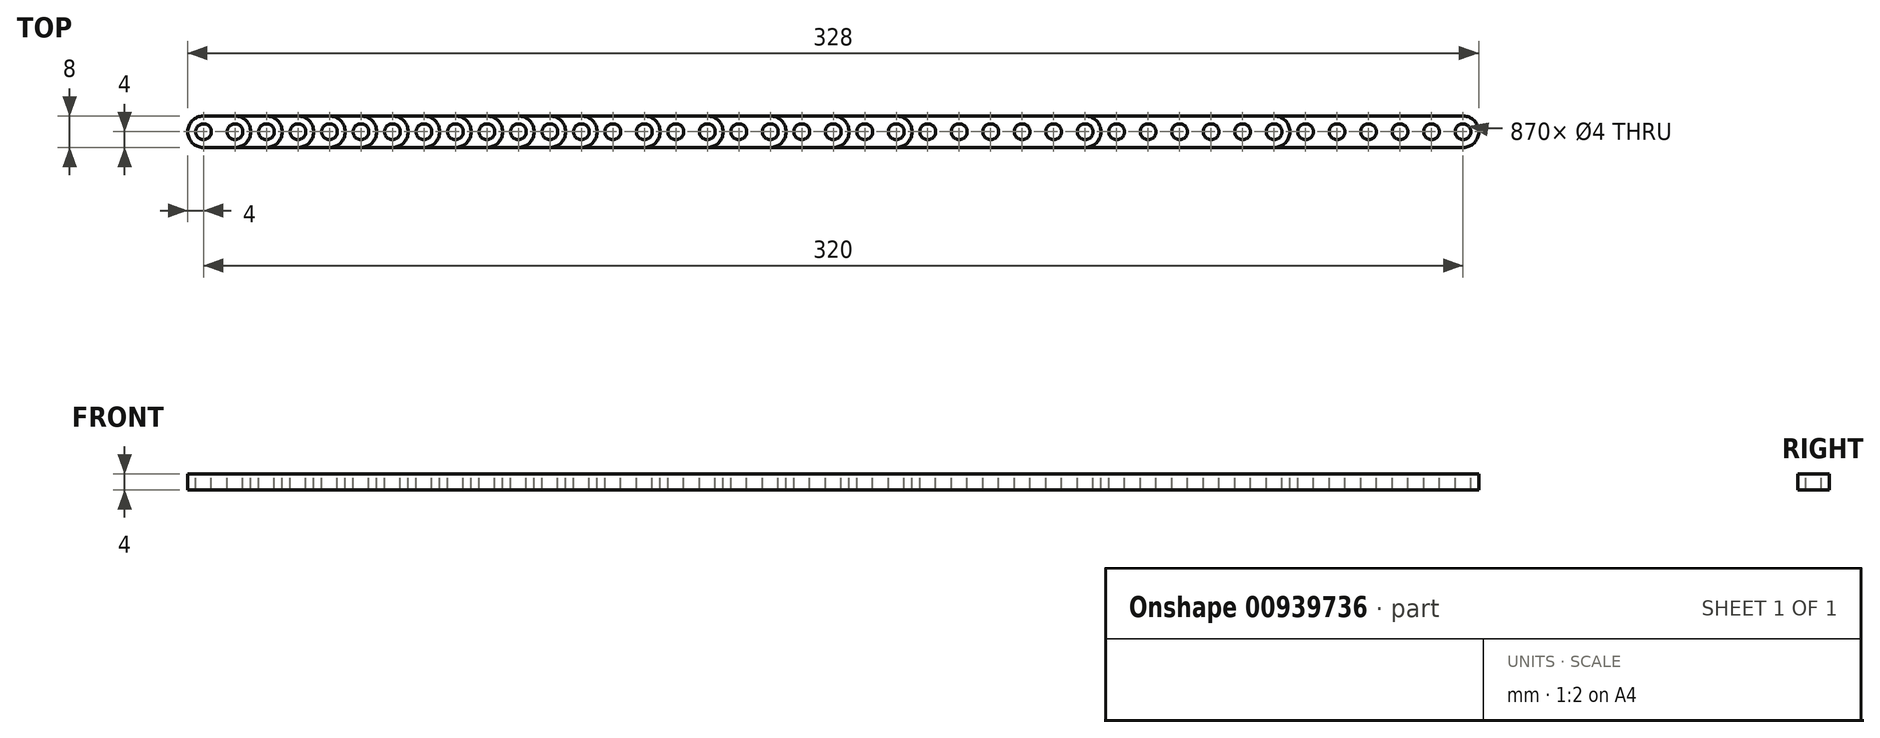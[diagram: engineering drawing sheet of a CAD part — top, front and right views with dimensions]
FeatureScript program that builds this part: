
annotation { "Feature Type Name" : "Feature", "Feature Type Description" : "" }
export const myFeature = defineFeature(function(context is Context, id is Id, definition is map)
    precondition{}
    {
        {
            var Q0;
            Q0=qCreatedBy(makeId("Right.planeOp"),FACE);
            var sketch = newSketch(context, id + "F0", { "sketchPlane" : qUnion([Q0])});
            skLineSegment(sketch, "E0.bottom", {"start": v(4, 2) * mm, "end": v(-4, 2) * mm});
            skLineSegment(sketch, "E0.top", {"start": v(4, -2) * mm, "end": v(-4, -2) * mm});
            skLineSegment(sketch, "E0.left", {"start": v(4, 2) * mm, "end": v(4, -2) * mm});
            skLineSegment(sketch, "E0.right", {"start": v(-4, 2) * mm, "end": v(-4, -2) * mm});
            skPoint(sketch, "E0.middle", {"position": v(0, 0) * mm});
            skSolve(sketch);
        }
        {
            var Q0;
            Q0=qSketchRegion(id+"F0",true);
            extrude(context, id + "F1", {"entities" : qUnion([Q0]), "depth" : 16 * mm, "offsetDistance" : 25 * mm});
        }
        {
            var Q0;
            Q0=qSketchRegion(id+"F0",true);
            extrude(context, id + "F2", {"entities" : qUnion([Q0]), "depth" : 24 * mm, "offsetDistance" : 25 * mm});
        }
        {
            var Q0;
            Q0=qSketchRegion(id+"F0",true);
            extrude(context, id + "F3", {"entities" : qUnion([Q0]), "depth" : 32 * mm, "offsetDistance" : 25 * mm});
        }
        {
            var Q0;
            Q0=qSketchRegion(id+"F0",true);
            extrude(context, id + "F4", {"entities" : qUnion([Q0]), "depth" : 40 * mm, "offsetDistance" : 25 * mm});
        }
        {
            var Q0;
            Q0=qSketchRegion(id+"F0",true);
            extrude(context, id + "F5", {"entities" : qUnion([Q0]), "depth" : 48 * mm, "offsetDistance" : 25 * mm});
        }
        {
            var Q0;
            Q0=qSketchRegion(id+"F0",true);
            extrude(context, id + "F6", {"entities" : qUnion([Q0]), "depth" : 56 * mm, "offsetDistance" : 25 * mm});
        }
        {
            var Q0;
            Q0=qSketchRegion(id+"F0",true);
            extrude(context, id + "F7", {"entities" : qUnion([Q0]), "depth" : 64 * mm, "offsetDistance" : 25 * mm});
        }
        {
            var Q0;
            Q0=qSketchRegion(id+"F0",true);
            extrude(context, id + "F8", {"entities" : qUnion([Q0]), "depth" : 72 * mm, "offsetDistance" : 25 * mm});
        }
        {
            var Q0;
            Q0=qSketchRegion(id+"F0",true);
            extrude(context, id + "F9", {"entities" : qUnion([Q0]), "depth" : 80 * mm, "offsetDistance" : 25 * mm});
        }
        {
            var Q0;
            Q0=qSketchRegion(id+"F0",true);
            extrude(context, id + "F10", {"entities" : qUnion([Q0]), "depth" : 88 * mm, "offsetDistance" : 25 * mm});
        }
        {
            var Q0;
            Q0=qSketchRegion(id+"F0",true);
            extrude(context, id + "F11", {"entities" : qUnion([Q0]), "depth" : 96 * mm, "offsetDistance" : 25 * mm});
        }
        {
            var Q0;
            Q0=qSketchRegion(id+"F0",true);
            extrude(context, id + "F12", {"entities" : qUnion([Q0]), "depth" : 104 * mm, "offsetDistance" : 25 * mm});
        }
        {
            var Q0;
            Q0=qSketchRegion(id+"F0",true);
            extrude(context, id + "F13", {"entities" : qUnion([Q0]), "depth" : 120 * mm, "offsetDistance" : 25 * mm});
        }
        {
            var Q0;
            Q0=qSketchRegion(id+"F0",true);
            extrude(context, id + "F14", {"entities" : qUnion([Q0]), "depth" : 136 * mm, "offsetDistance" : 25 * mm});
        }
        {
            var Q0;
            Q0=qSketchRegion(id+"F0",true);
            extrude(context, id + "F15", {"entities" : qUnion([Q0]), "depth" : 152 * mm, "offsetDistance" : 25 * mm});
        }
        {
            var Q0;
            Q0=qSketchRegion(id+"F0",true);
            extrude(context, id + "F16", {"entities" : qUnion([Q0]), "depth" : 168 * mm, "offsetDistance" : 25 * mm});
        }
        {
            var Q0;
            Q0=qSketchRegion(id+"F0",true);
            extrude(context, id + "F17", {"entities" : qUnion([Q0]), "depth" : 184 * mm, "offsetDistance" : 25 * mm});
        }
        {
            var Q0;
            Q0=qSketchRegion(id+"F0",true);
            extrude(context, id + "F18", {"entities" : qUnion([Q0]), "depth" : 232 * mm, "offsetDistance" : 25 * mm});
        }
        {
            var Q0;
            Q0=qSketchRegion(id+"F0",true);
            extrude(context, id + "F19", {"entities" : qUnion([Q0]), "depth" : 280 * mm, "offsetDistance" : 25 * mm});
        }
        {
            var Q0;
            Q0=qSketchRegion(id+"F0",true);
            extrude(context, id + "F20", {"entities" : qUnion([Q0]), "depth" : 328 * mm, "offsetDistance" : 25 * mm});
        }
        {
            var Q0;
            Q0=qCreatedBy(makeId("Top.planeOp"),FACE);
            var sketch = newSketch(context, id + "F21", { "sketchPlane" : qUnion([Q0])});
            skCircle(sketch, "E1", {"center": v(4, 0) * mm, "radius": 2 * mm});
            skCircle(sketch, "E2.1.0.0", {"center": v(12, 0) * mm, "radius": 2 * mm});
            skCircle(sketch, "E2.2.0.0", {"center": v(20, 0) * mm, "radius": 2 * mm});
            skCircle(sketch, "E2.3.0.0", {"center": v(28, 0) * mm, "radius": 2 * mm});
            skCircle(sketch, "E2.4.0.0", {"center": v(36, 0) * mm, "radius": 2 * mm});
            skCircle(sketch, "E2.5.0.0", {"center": v(44, 0) * mm, "radius": 2 * mm});
            skCircle(sketch, "E2.6.0.0", {"center": v(52, 0) * mm, "radius": 2 * mm});
            skCircle(sketch, "E2.7.0.0", {"center": v(60, 0) * mm, "radius": 2 * mm});
            skCircle(sketch, "E2.8.0.0", {"center": v(68, 0) * mm, "radius": 2 * mm});
            skCircle(sketch, "E2.9.0.0", {"center": v(76, 0) * mm, "radius": 2 * mm});
            skCircle(sketch, "E2.10.0.0", {"center": v(84, 0) * mm, "radius": 2 * mm});
            skCircle(sketch, "E2.11.0.0", {"center": v(92, 0) * mm, "radius": 2 * mm});
            skCircle(sketch, "E2.12.0.0", {"center": v(100, 0) * mm, "radius": 2 * mm});
            skCircle(sketch, "E2.13.0.0", {"center": v(108, 0) * mm, "radius": 2 * mm});
            skCircle(sketch, "E2.14.0.0", {"center": v(116, 0) * mm, "radius": 2 * mm});
            skCircle(sketch, "E2.15.0.0", {"center": v(124, 0) * mm, "radius": 2 * mm});
            skCircle(sketch, "E2.16.0.0", {"center": v(132, 0) * mm, "radius": 2 * mm});
            skCircle(sketch, "E2.17.0.0", {"center": v(140, 0) * mm, "radius": 2 * mm});
            skCircle(sketch, "E2.18.0.0", {"center": v(148, 0) * mm, "radius": 2 * mm});
            skCircle(sketch, "E2.19.0.0", {"center": v(156, 0) * mm, "radius": 2 * mm});
            skCircle(sketch, "E2.20.0.0", {"center": v(164, 0) * mm, "radius": 2 * mm});
            skCircle(sketch, "E2.21.0.0", {"center": v(172, 0) * mm, "radius": 2 * mm});
            skCircle(sketch, "E2.22.0.0", {"center": v(180, 0) * mm, "radius": 2 * mm});
            skCircle(sketch, "E2.23.0.0", {"center": v(188, 0) * mm, "radius": 2 * mm});
            skCircle(sketch, "E2.24.0.0", {"center": v(196, 0) * mm, "radius": 2 * mm});
            skCircle(sketch, "E2.25.0.0", {"center": v(204, 0) * mm, "radius": 2 * mm});
            skCircle(sketch, "E2.26.0.0", {"center": v(212, 0) * mm, "radius": 2 * mm});
            skCircle(sketch, "E2.27.0.0", {"center": v(220, 0) * mm, "radius": 2 * mm});
            skCircle(sketch, "E2.28.0.0", {"center": v(228, 0) * mm, "radius": 2 * mm});
            skCircle(sketch, "E2.29.0.0", {"center": v(236, 0) * mm, "radius": 2 * mm});
            skCircle(sketch, "E2.30.0.0", {"center": v(244, 0) * mm, "radius": 2 * mm});
            skCircle(sketch, "E2.31.0.0", {"center": v(252, 0) * mm, "radius": 2 * mm});
            skCircle(sketch, "E2.32.0.0", {"center": v(260, 0) * mm, "radius": 2 * mm});
            skCircle(sketch, "E2.33.0.0", {"center": v(268, 0) * mm, "radius": 2 * mm});
            skCircle(sketch, "E2.34.0.0", {"center": v(276, 0) * mm, "radius": 2 * mm});
            skCircle(sketch, "E2.35.0.0", {"center": v(284, 0) * mm, "radius": 2 * mm});
            skCircle(sketch, "E2.36.0.0", {"center": v(292, 0) * mm, "radius": 2 * mm});
            skCircle(sketch, "E2.37.0.0", {"center": v(300, 0) * mm, "radius": 2 * mm});
            skCircle(sketch, "E2.38.0.0", {"center": v(308, 0) * mm, "radius": 2 * mm});
            skCircle(sketch, "E2.39.0.0", {"center": v(316, 0) * mm, "radius": 2 * mm});
            skCircle(sketch, "E2.40.0.0", {"center": v(324, 0) * mm, "radius": 2 * mm});
            skLineSegment(sketch, "E2.direction1", {"start": v(4, 0) * mm, "end": v(12, 0) * mm, "construction": true});
            skLineSegment(sketch, "E3.0", {"start": v(0, 4) * mm, "end": v(0, -4) * mm});
            skLineSegment(sketch, "E4.0", {"start": v(4, -4) * mm, "end": v(0, -4) * mm, "construction": true});
            skLineSegment(sketch, "E5.0", {"start": v(4, 4) * mm, "end": v(0, 4) * mm, "construction": true});
            skArc(sketch, "E6", {"start": v(4, -4) * mm, "mid": v(0, 0) * mm, "end": v(4, 4) * mm});
            skPoint(sketch, "E7.orphan", {"position": v(16, -4) * mm});
            skPoint(sketch, "E8.orphan", {"position": v(16, 4) * mm});
            skLineSegment(sketch, "E9", {"start": v(0, -4) * mm, "end": v(4, -4) * mm});
            skLineSegment(sketch, "E10", {"start": v(0, 4) * mm, "end": v(4, 4) * mm});
            skSolve(sketch);
        }
        {
            var Q0;
            Q0=qSketchRegion(id+"F21",true);
            extrude(context, id + "F22", {"entities" : qUnion([Q0]), "operationType" : NewBodyOperationType.REMOVE, "oppositeDirection" : true, "depth" : 25 * mm, "offsetDistance" : 25 * mm, "symmetric" : true});
        }
        {
            var Q0;
            Q0=makeQuery(id+"F20.opExtrude","CAP_EDGE",EDGE,{"disambiguationData":[OSD([sQuery(id+"F0.wireOp",EDGE,"E0.right")])],"isStart":false});
            var Q1;
            Q1=makeQuery(id+"F20.opExtrude","CAP_EDGE",EDGE,{"disambiguationData":[OSD([sQuery(id+"F0.wireOp",EDGE,"E0.left")])],"isStart":false});
            var Q2;
            Q2=makeQuery(id+"F19.opExtrude","CAP_EDGE",EDGE,{"disambiguationData":[OSD([sQuery(id+"F0.wireOp",EDGE,"E0.right")])],"isStart":false});
            var Q3;
            Q3=makeQuery(id+"F19.opExtrude","CAP_EDGE",EDGE,{"disambiguationData":[OSD([sQuery(id+"F0.wireOp",EDGE,"E0.left")])],"isStart":false});
            var Q4;
            Q4=makeQuery(id+"F18.opExtrude","CAP_EDGE",EDGE,{"disambiguationData":[OSD([sQuery(id+"F0.wireOp",EDGE,"E0.right")])],"isStart":false});
            var Q5;
            Q5=makeQuery(id+"F17.opExtrude","CAP_EDGE",EDGE,{"disambiguationData":[OSD([sQuery(id+"F0.wireOp",EDGE,"E0.right")])],"isStart":false});
            var Q6;
            Q6=makeQuery(id+"F16.opExtrude","CAP_EDGE",EDGE,{"disambiguationData":[OSD([sQuery(id+"F0.wireOp",EDGE,"E0.right")])],"isStart":false});
            var Q7;
            Q7=makeQuery(id+"F15.opExtrude","CAP_EDGE",EDGE,{"disambiguationData":[OSD([sQuery(id+"F0.wireOp",EDGE,"E0.right")])],"isStart":false});
            var Q8;
            Q8=makeQuery(id+"F14.opExtrude","CAP_EDGE",EDGE,{"disambiguationData":[OSD([sQuery(id+"F0.wireOp",EDGE,"E0.right")])],"isStart":false});
            var Q9;
            Q9=makeQuery(id+"F13.opExtrude","CAP_EDGE",EDGE,{"disambiguationData":[OSD([sQuery(id+"F0.wireOp",EDGE,"E0.right")])],"isStart":false});
            var Q10;
            Q10=makeQuery(id+"F12.opExtrude","CAP_EDGE",EDGE,{"disambiguationData":[OSD([sQuery(id+"F0.wireOp",EDGE,"E0.right")])],"isStart":false});
            var Q11;
            Q11=makeQuery(id+"F11.opExtrude","CAP_EDGE",EDGE,{"disambiguationData":[OSD([sQuery(id+"F0.wireOp",EDGE,"E0.right")])],"isStart":false});
            var Q12;
            Q12=makeQuery(id+"F10.opExtrude","CAP_EDGE",EDGE,{"disambiguationData":[OSD([sQuery(id+"F0.wireOp",EDGE,"E0.right")])],"isStart":false});
            var Q13;
            Q13=makeQuery(id+"F9.opExtrude","CAP_EDGE",EDGE,{"disambiguationData":[OSD([sQuery(id+"F0.wireOp",EDGE,"E0.right")])],"isStart":false});
            var Q14;
            Q14=makeQuery(id+"F8.opExtrude","CAP_EDGE",EDGE,{"disambiguationData":[OSD([sQuery(id+"F0.wireOp",EDGE,"E0.right")])],"isStart":false});
            var Q15;
            Q15=makeQuery(id+"F7.opExtrude","CAP_EDGE",EDGE,{"disambiguationData":[OSD([sQuery(id+"F0.wireOp",EDGE,"E0.right")])],"isStart":false});
            var Q16;
            Q16=makeQuery(id+"F6.opExtrude","CAP_EDGE",EDGE,{"disambiguationData":[OSD([sQuery(id+"F0.wireOp",EDGE,"E0.right")])],"isStart":false});
            var Q17;
            Q17=makeQuery(id+"F5.opExtrude","CAP_EDGE",EDGE,{"disambiguationData":[OSD([sQuery(id+"F0.wireOp",EDGE,"E0.right")])],"isStart":false});
            var Q18;
            Q18=makeQuery(id+"F4.opExtrude","CAP_EDGE",EDGE,{"disambiguationData":[OSD([sQuery(id+"F0.wireOp",EDGE,"E0.right")])],"isStart":false});
            var Q19;
            Q19=makeQuery(id+"F3.opExtrude","CAP_EDGE",EDGE,{"disambiguationData":[OSD([sQuery(id+"F0.wireOp",EDGE,"E0.right")])],"isStart":false});
            var Q20;
            Q20=makeQuery(id+"F2.opExtrude","CAP_EDGE",EDGE,{"disambiguationData":[OSD([sQuery(id+"F0.wireOp",EDGE,"E0.right")])],"isStart":false});
            var Q21;
            Q21=makeQuery(id+"F1.opExtrude","CAP_EDGE",EDGE,{"disambiguationData":[OSD([sQuery(id+"F0.wireOp",EDGE,"E0.right")])],"isStart":false});
            var Q22;
            Q22=makeQuery(id+"F18.opExtrude","CAP_EDGE",EDGE,{"disambiguationData":[OSD([sQuery(id+"F0.wireOp",EDGE,"E0.left")])],"isStart":false});
            var Q23;
            Q23=makeQuery(id+"F17.opExtrude","CAP_EDGE",EDGE,{"disambiguationData":[OSD([sQuery(id+"F0.wireOp",EDGE,"E0.left")])],"isStart":false});
            var Q24;
            Q24=makeQuery(id+"F16.opExtrude","CAP_EDGE",EDGE,{"disambiguationData":[OSD([sQuery(id+"F0.wireOp",EDGE,"E0.left")])],"isStart":false});
            var Q25;
            Q25=makeQuery(id+"F15.opExtrude","CAP_EDGE",EDGE,{"disambiguationData":[OSD([sQuery(id+"F0.wireOp",EDGE,"E0.left")])],"isStart":false});
            var Q26;
            Q26=makeQuery(id+"F14.opExtrude","CAP_EDGE",EDGE,{"disambiguationData":[OSD([sQuery(id+"F0.wireOp",EDGE,"E0.left")])],"isStart":false});
            var Q27;
            Q27=makeQuery(id+"F13.opExtrude","CAP_EDGE",EDGE,{"disambiguationData":[OSD([sQuery(id+"F0.wireOp",EDGE,"E0.left")])],"isStart":false});
            var Q28;
            Q28=makeQuery(id+"F12.opExtrude","CAP_EDGE",EDGE,{"disambiguationData":[OSD([sQuery(id+"F0.wireOp",EDGE,"E0.left")])],"isStart":false});
            var Q29;
            Q29=makeQuery(id+"F11.opExtrude","CAP_EDGE",EDGE,{"disambiguationData":[OSD([sQuery(id+"F0.wireOp",EDGE,"E0.left")])],"isStart":false});
            var Q30;
            Q30=makeQuery(id+"F10.opExtrude","CAP_EDGE",EDGE,{"disambiguationData":[OSD([sQuery(id+"F0.wireOp",EDGE,"E0.left")])],"isStart":false});
            var Q31;
            Q31=makeQuery(id+"F9.opExtrude","CAP_EDGE",EDGE,{"disambiguationData":[OSD([sQuery(id+"F0.wireOp",EDGE,"E0.left")])],"isStart":false});
            var Q32;
            Q32=makeQuery(id+"F8.opExtrude","CAP_EDGE",EDGE,{"disambiguationData":[OSD([sQuery(id+"F0.wireOp",EDGE,"E0.left")])],"isStart":false});
            var Q33;
            Q33=makeQuery(id+"F7.opExtrude","CAP_EDGE",EDGE,{"disambiguationData":[OSD([sQuery(id+"F0.wireOp",EDGE,"E0.left")])],"isStart":false});
            var Q34;
            Q34=makeQuery(id+"F6.opExtrude","CAP_EDGE",EDGE,{"disambiguationData":[OSD([sQuery(id+"F0.wireOp",EDGE,"E0.left")])],"isStart":false});
            var Q35;
            Q35=makeQuery(id+"F5.opExtrude","CAP_EDGE",EDGE,{"disambiguationData":[OSD([sQuery(id+"F0.wireOp",EDGE,"E0.left")])],"isStart":false});
            var Q36;
            Q36=makeQuery(id+"F4.opExtrude","CAP_EDGE",EDGE,{"disambiguationData":[OSD([sQuery(id+"F0.wireOp",EDGE,"E0.left")])],"isStart":false});
            var Q37;
            Q37=makeQuery(id+"F3.opExtrude","CAP_EDGE",EDGE,{"disambiguationData":[OSD([sQuery(id+"F0.wireOp",EDGE,"E0.left")])],"isStart":false});
            var Q38;
            Q38=makeQuery(id+"F2.opExtrude","CAP_EDGE",EDGE,{"disambiguationData":[OSD([sQuery(id+"F0.wireOp",EDGE,"E0.left")])],"isStart":false});
            var Q39;
            Q39=makeQuery(id+"F1.opExtrude","CAP_EDGE",EDGE,{"disambiguationData":[OSD([sQuery(id+"F0.wireOp",EDGE,"E0.left")])],"isStart":false});
            fillet(context, id + "F23", {"entities" : qUnion([Q0, Q1, Q2, Q3, Q4, Q5, Q6, Q7, Q8, Q9, Q10, Q11, Q12, Q13, Q14, Q15, Q16, Q17, Q18, Q19, Q20, Q21, Q22, Q23, Q24, Q25, Q26, Q27, Q28, Q29, Q30, Q31, Q32, Q33, Q34, Q35, Q36, Q37, Q38, Q39]), "radius" : 4 * mm, "tangentPropagation" : true, "allowEdgeOverflow" : false});
        }
    });
